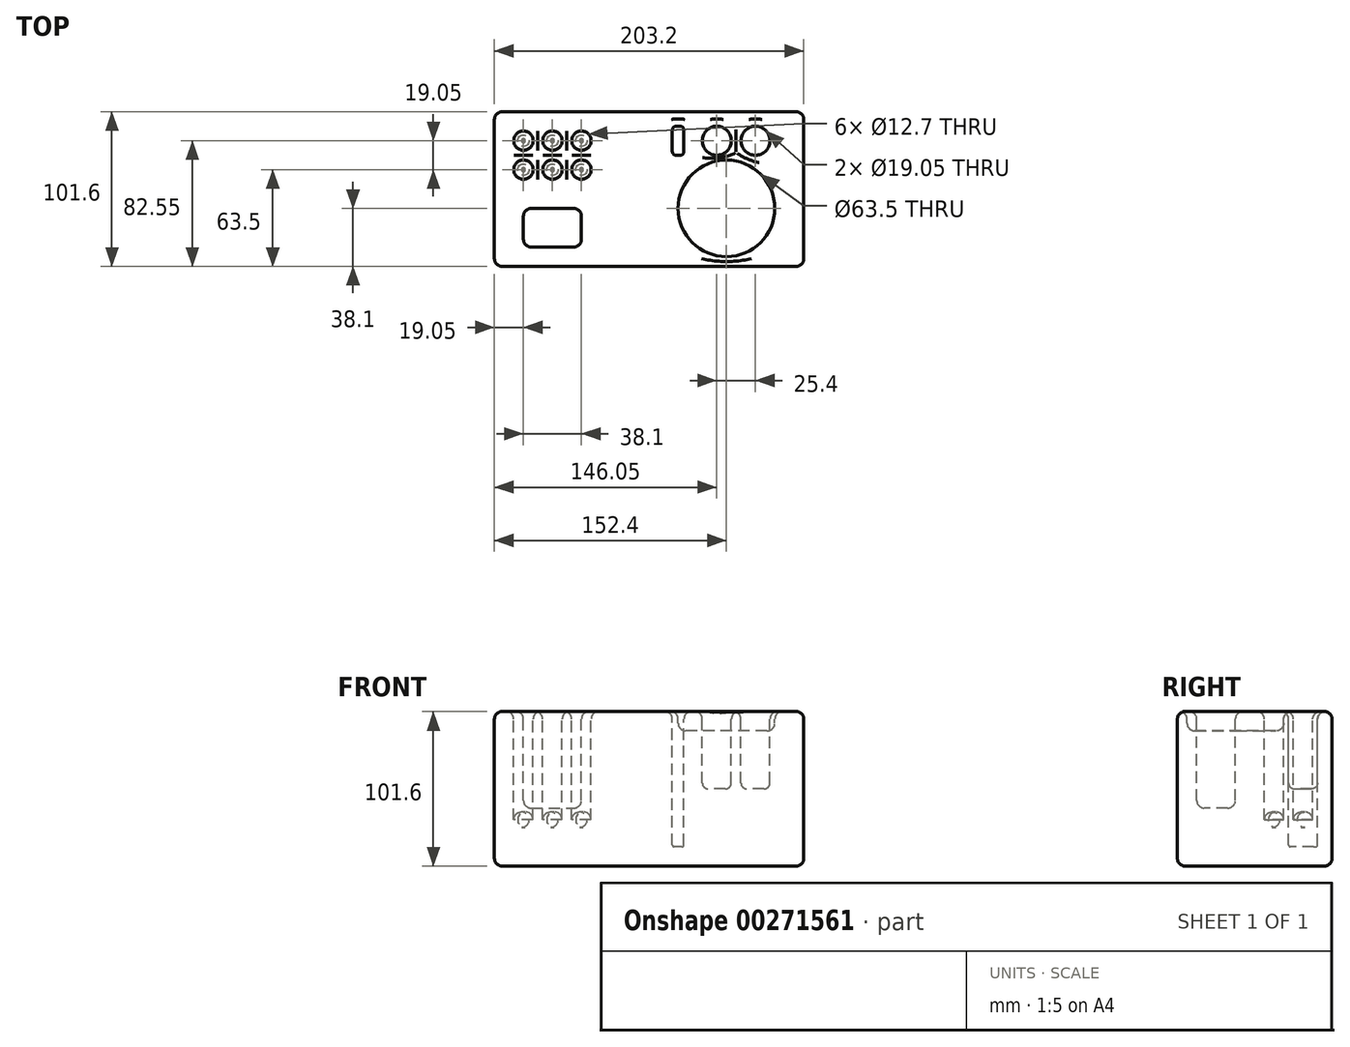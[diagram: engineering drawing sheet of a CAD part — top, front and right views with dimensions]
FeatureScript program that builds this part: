
annotation { "Feature Type Name" : "Feature", "Feature Type Description" : "" }
export const myFeature = defineFeature(function(context is Context, id is Id, definition is map)
    precondition{}
    {
        {
            var Q0;
            Q0=qCreatedBy(makeId("Top.planeOp"),FACE);
            var sketch = newSketch(context, id + "F0", { "sketchPlane" : qUnion([Q0])});
            skLineSegment(sketch, "E0.bottom", {"start": v(0, 0) * mm, "end": v(-203.2, 0) * mm});
            skLineSegment(sketch, "E0.top", {"start": v(0, 101.6) * mm, "end": v(-203.2, 101.6) * mm});
            skLineSegment(sketch, "E0.left", {"start": v(0, 0) * mm, "end": v(0, 101.6) * mm});
            skLineSegment(sketch, "E0.right", {"start": v(-203.2, 0) * mm, "end": v(-203.2, 101.6) * mm});
            skPoint(sketch, "E1", {"position": v(-165.1, 101.6) * mm});
            skPoint(sketch, "E2", {"position": v(-146.05, 101.6) * mm});
            skPoint(sketch, "E3", {"position": v(-184.15, 101.6) * mm});
            skPoint(sketch, "E4", {"position": v(-101.6, 101.6) * mm});
            skPoint(sketch, "E5", {"position": v(-203.2, 82.55) * mm});
            skPoint(sketch, "E6", {"position": v(-203.2, 63.5) * mm});
            skCircle(sketch, "E7", {"center": v(-184.15, 82.55) * mm, "radius": 6.35 * mm});
            skCircle(sketch, "E8", {"center": v(-165.1, 63.5) * mm, "radius": 6.35 * mm});
            skCircle(sketch, "E9", {"center": v(-165.1, 82.55) * mm, "radius": 6.35 * mm});
            skCircle(sketch, "E10", {"center": v(-146.05, 82.55) * mm, "radius": 6.35 * mm});
            skCircle(sketch, "E11", {"center": v(-146.05, 63.5) * mm, "radius": 6.35 * mm});
            skCircle(sketch, "E12", {"center": v(-184.15, 63.5) * mm, "radius": 6.35 * mm});
            skPoint(sketch, "E13", {"position": v(-203.2, 12.7) * mm});
            skPoint(sketch, "E14", {"position": v(-203.2, 38.1) * mm});
            skPoint(sketch, "E15", {"position": v(-184.15, 38.1) * mm});
            skPoint(sketch, "E16", {"position": v(-146.05, 12.7) * mm});
            skLineSegment(sketch, "E17.bottom", {"start": v(-184.15, 38.1) * mm, "end": v(-146.05, 38.1) * mm});
            skLineSegment(sketch, "E17.top", {"start": v(-184.15, 12.7) * mm, "end": v(-146.05, 12.7) * mm});
            skLineSegment(sketch, "E17.left", {"start": v(-184.15, 38.1) * mm, "end": v(-184.15, 12.7) * mm});
            skLineSegment(sketch, "E17.right", {"start": v(-146.05, 38.1) * mm, "end": v(-146.05, 12.7) * mm});
            skPoint(sketch, "E18", {"position": v(-82.55, 101.6) * mm});
            skPoint(sketch, "E19", {"position": v(-82.55, 82.55) * mm});
            skLineSegment(sketch, "E20.bottom", {"start": v(-78.74, 92.07) * mm, "end": v(-86.36, 92.07) * mm});
            skLineSegment(sketch, "E20.top", {"start": v(-78.74, 73.02) * mm, "end": v(-86.36, 73.02) * mm});
            skLineSegment(sketch, "E20.left", {"start": v(-78.74, 92.07) * mm, "end": v(-78.74, 73.02) * mm});
            skLineSegment(sketch, "E20.right", {"start": v(-86.36, 92.07) * mm, "end": v(-86.36, 73.02) * mm});
            skPoint(sketch, "E21", {"position": v(-57.15, 101.6) * mm});
            skPoint(sketch, "E22", {"position": v(-31.75, 101.6) * mm});
            skCircle(sketch, "E23", {"center": v(-57.15, 82.55) * mm, "radius": 9.53 * mm});
            skPoint(sketch, "E23.centerSnap0", {"position": v(-78.74, 82.55) * mm});
            skCircle(sketch, "E24", {"center": v(-31.75, 82.55) * mm, "radius": 9.53 * mm});
            skPoint(sketch, "E25", {"position": v(-50.8, 101.6) * mm});
            skPoint(sketch, "E26", {"position": v(0, 38.1) * mm});
            skCircle(sketch, "E27", {"center": v(-50.8, 38.1) * mm, "radius": 31.75 * mm});
            skSolve(sketch);
        }
        {
            var Q0;
            Q0=makeQuery(id+"F0.imprint","IMPRINT",FACE,{"disambiguationData":[TD([[makeQuery(id+"F0.imprint","IMPRINT",EDGE,{"derivedFrom":sQuery(id+"F0.wireOp",EDGE,"E0.bottom")}),-1.0]])]});
            var Q1;
            Q1=makeQuery(id+"F0.imprint","IMPRINT",FACE,{"disambiguationData":[TD([[makeQuery(id+"F0.imprint","IMPRINT",EDGE,{"derivedFrom":sQuery(id+"F0.wireOp",EDGE,"E9")}),1.0]])]});
            var Q2;
            Q2=makeQuery(id+"F0.imprint","IMPRINT",FACE,{"disambiguationData":[TD([[makeQuery(id+"F0.imprint","IMPRINT",EDGE,{"derivedFrom":sQuery(id+"F0.wireOp",EDGE,"E7")}),1.0]])]});
            var Q3;
            Q3=makeQuery(id+"F0.imprint","IMPRINT",FACE,{"disambiguationData":[TD([[makeQuery(id+"F0.imprint","IMPRINT",EDGE,{"derivedFrom":sQuery(id+"F0.wireOp",EDGE,"E8")}),1.0]])]});
            var Q4;
            Q4=makeQuery(id+"F0.imprint","IMPRINT",FACE,{"disambiguationData":[TD([[makeQuery(id+"F0.imprint","IMPRINT",EDGE,{"derivedFrom":sQuery(id+"F0.wireOp",EDGE,"E12")}),1.0]])]});
            var Q5;
            Q5=makeQuery(id+"F0.imprint","IMPRINT",FACE,{"disambiguationData":[TD([[makeQuery(id+"F0.imprint","IMPRINT",EDGE,{"derivedFrom":sQuery(id+"F0.wireOp",EDGE,"E11")}),1.0]])]});
            var Q6;
            Q6=makeQuery(id+"F0.imprint","IMPRINT",FACE,{"disambiguationData":[TD([[makeQuery(id+"F0.imprint","IMPRINT",EDGE,{"derivedFrom":sQuery(id+"F0.wireOp",EDGE,"E10")}),1.0]])]});
            var Q7;
            Q7=makeQuery(id+"F0.imprint","IMPRINT",FACE,{"disambiguationData":[TD([[makeQuery(id+"F0.imprint","IMPRINT",EDGE,{"derivedFrom":sQuery(id+"F0.wireOp",EDGE,"E17.bottom")}),-1.0]])]});
            var Q8;
            Q8=makeQuery(id+"F0.imprint","IMPRINT",FACE,{"disambiguationData":[TD([[makeQuery(id+"F0.imprint","IMPRINT",EDGE,{"derivedFrom":sQuery(id+"F0.wireOp",EDGE,"E27")}),1.0]])]});
            var Q9;
            Q9=makeQuery(id+"F0.imprint","IMPRINT",FACE,{"disambiguationData":[TD([[makeQuery(id+"F0.imprint","IMPRINT",EDGE,{"derivedFrom":sQuery(id+"F0.wireOp",EDGE,"E23")}),1.0]])]});
            var Q10;
            Q10=makeQuery(id+"F0.imprint","IMPRINT",FACE,{"disambiguationData":[TD([[makeQuery(id+"F0.imprint","IMPRINT",EDGE,{"derivedFrom":sQuery(id+"F0.wireOp",EDGE,"E24")}),1.0]])]});
            var Q11;
            Q11=makeQuery(id+"F0.imprint","IMPRINT",FACE,{"disambiguationData":[TD([[makeQuery(id+"F0.imprint","IMPRINT",EDGE,{"derivedFrom":sQuery(id+"F0.wireOp",EDGE,"E20.bottom")}),1.0]])]});
            extrude(context, id + "F1", {"entities" : qUnion([Q0, Q1, Q2, Q3, Q4, Q5, Q6, Q7, Q8, Q9, Q10, Q11]), "oppositeDirection" : true, "depth" : 101.6 * mm});
        }
        {
            var Q0;
            Q0=makeQuery(id+"F0.imprint","IMPRINT",FACE,{"disambiguationData":[TD([[makeQuery(id+"F0.imprint","IMPRINT",EDGE,{"derivedFrom":sQuery(id+"F0.wireOp",EDGE,"E27")}),1.0]])]});
            extrude(context, id + "F2", {"entities" : qUnion([Q0]), "operationType" : NewBodyOperationType.REMOVE, "oppositeDirection" : true, "depth" : 12.7 * mm});
        }
        {
            var Q0;
            Q0=makeQuery(id+"F0.imprint","IMPRINT",FACE,{"disambiguationData":[TD([[makeQuery(id+"F0.imprint","IMPRINT",EDGE,{"derivedFrom":sQuery(id+"F0.wireOp",EDGE,"E23")}),1.0]])]});
            var Q1;
            Q1=makeQuery(id+"F0.imprint","IMPRINT",FACE,{"disambiguationData":[TD([[makeQuery(id+"F0.imprint","IMPRINT",EDGE,{"derivedFrom":sQuery(id+"F0.wireOp",EDGE,"E24")}),1.0]])]});
            extrude(context, id + "F3", {"entities" : qUnion([Q0, Q1]), "operationType" : NewBodyOperationType.REMOVE, "oppositeDirection" : true, "depth" : 50.8 * mm});
        }
        {
            var Q0;
            Q0=makeQuery(id+"F0.imprint","IMPRINT",FACE,{"disambiguationData":[TD([[makeQuery(id+"F0.imprint","IMPRINT",EDGE,{"derivedFrom":sQuery(id+"F0.wireOp",EDGE,"E20.bottom")}),1.0]])]});
            extrude(context, id + "F4", {"entities" : qUnion([Q0]), "operationType" : NewBodyOperationType.REMOVE, "oppositeDirection" : true, "depth" : 88.9 * mm});
        }
        {
            var Q0;
            Q0=makeQuery(id+"F0.imprint","IMPRINT",FACE,{"disambiguationData":[TD([[makeQuery(id+"F0.imprint","IMPRINT",EDGE,{"derivedFrom":sQuery(id+"F0.wireOp",EDGE,"E12")}),1.0]])]});
            var Q1;
            Q1=makeQuery(id+"F0.imprint","IMPRINT",FACE,{"disambiguationData":[TD([[makeQuery(id+"F0.imprint","IMPRINT",EDGE,{"derivedFrom":sQuery(id+"F0.wireOp",EDGE,"E7")}),1.0]])]});
            var Q2;
            Q2=makeQuery(id+"F0.imprint","IMPRINT",FACE,{"disambiguationData":[TD([[makeQuery(id+"F0.imprint","IMPRINT",EDGE,{"derivedFrom":sQuery(id+"F0.wireOp",EDGE,"E8")}),1.0]])]});
            var Q3;
            Q3=makeQuery(id+"F0.imprint","IMPRINT",FACE,{"disambiguationData":[TD([[makeQuery(id+"F0.imprint","IMPRINT",EDGE,{"derivedFrom":sQuery(id+"F0.wireOp",EDGE,"E10")}),1.0]])]});
            var Q4;
            Q4=makeQuery(id+"F0.imprint","IMPRINT",FACE,{"disambiguationData":[TD([[makeQuery(id+"F0.imprint","IMPRINT",EDGE,{"derivedFrom":sQuery(id+"F0.wireOp",EDGE,"E11")}),1.0]])]});
            var Q5;
            Q5=makeQuery(id+"F0.imprint","IMPRINT",FACE,{"disambiguationData":[TD([[makeQuery(id+"F0.imprint","IMPRINT",EDGE,{"derivedFrom":sQuery(id+"F0.wireOp",EDGE,"E9")}),1.0]])]});
            extrude(context, id + "F5", {"entities" : qUnion([Q0, Q1, Q2, Q3, Q4, Q5]), "operationType" : NewBodyOperationType.REMOVE, "oppositeDirection" : true, "depth" : 76.2 * mm});
        }
        {
            var Q0;
            Q0=makeQuery(id+"F0.imprint","IMPRINT",FACE,{"disambiguationData":[TD([[makeQuery(id+"F0.imprint","IMPRINT",EDGE,{"derivedFrom":sQuery(id+"F0.wireOp",EDGE,"E17.bottom")}),-1.0]])]});
            extrude(context, id + "F6", {"entities" : qUnion([Q0]), "operationType" : NewBodyOperationType.REMOVE, "oppositeDirection" : true, "depth" : 63.5 * mm});
        }
        {
            var Q0;
            Q0=makeQuery(id+"F2.boolean.opBoolean","COPY",EDGE,{"derivedFrom":makeQuery(id+"F2.opExtrude","CAP_EDGE",EDGE,{"disambiguationData":[OSD([sQuery(id+"F0.wireOp",EDGE,"E27")])],"isStart":false})});
            fillet(context, id + "F7", {"entities" : qUnion([Q0]), "radius" : 5.08 * mm, "tangentPropagation" : true, "allowEdgeOverflow" : false});
        }
        {
            var Q0;
            Q0=makeQuery(id+"F5.boolean.opBoolean","COPY",EDGE,{"derivedFrom":makeQuery(id+"F5.opExtrude","CAP_EDGE",EDGE,{"disambiguationData":[OSD([sQuery(id+"F0.wireOp",EDGE,"E7")])],"isStart":false})});
            var Q1;
            Q1=makeQuery(id+"F5.boolean.opBoolean","COPY",EDGE,{"derivedFrom":makeQuery(id+"F5.opExtrude","CAP_EDGE",EDGE,{"disambiguationData":[OSD([sQuery(id+"F0.wireOp",EDGE,"E9")])],"isStart":false})});
            var Q2;
            Q2=makeQuery(id+"F5.boolean.opBoolean","COPY",EDGE,{"derivedFrom":makeQuery(id+"F5.opExtrude","CAP_EDGE",EDGE,{"disambiguationData":[OSD([sQuery(id+"F0.wireOp",EDGE,"E10")])],"isStart":false})});
            var Q3;
            Q3=makeQuery(id+"F5.boolean.opBoolean","COPY",EDGE,{"derivedFrom":makeQuery(id+"F5.opExtrude","CAP_EDGE",EDGE,{"disambiguationData":[OSD([sQuery(id+"F0.wireOp",EDGE,"E11")])],"isStart":false})});
            var Q4;
            Q4=makeQuery(id+"F5.boolean.opBoolean","COPY",EDGE,{"derivedFrom":makeQuery(id+"F5.opExtrude","CAP_EDGE",EDGE,{"disambiguationData":[OSD([sQuery(id+"F0.wireOp",EDGE,"E8")])],"isStart":false})});
            var Q5;
            Q5=makeQuery(id+"F5.boolean.opBoolean","COPY",EDGE,{"derivedFrom":makeQuery(id+"F5.opExtrude","CAP_EDGE",EDGE,{"disambiguationData":[OSD([sQuery(id+"F0.wireOp",EDGE,"E12")])],"isStart":false})});
            fillet(context, id + "F8", {"entities" : qUnion([Q0, Q1, Q2, Q3, Q4, Q5]), "radius" : 5.08 * mm, "tangentPropagation" : true, "allowEdgeOverflow" : false});
        }
        {
            var Q0;
            Q0=makeQuery(id+"F6.boolean.opBoolean","COPY",EDGE,{"derivedFrom":makeQuery(id+"F6.opExtrude","CAP_EDGE",EDGE,{"disambiguationData":[OSD([sQuery(id+"F0.wireOp",EDGE,"E17.right")])],"isStart":false})});
            var Q1;
            Q1=makeQuery(id+"F6.boolean.opBoolean","COPY",EDGE,{"derivedFrom":makeQuery(id+"F6.opExtrude","CAP_EDGE",EDGE,{"disambiguationData":[OSD([sQuery(id+"F0.wireOp",EDGE,"E17.bottom")])],"isStart":false})});
            var Q2;
            Q2=makeQuery(id+"F6.boolean.opBoolean","COPY",EDGE,{"derivedFrom":makeQuery(id+"F6.opExtrude","CAP_EDGE",EDGE,{"disambiguationData":[OSD([sQuery(id+"F0.wireOp",EDGE,"E17.left")])],"isStart":false})});
            var Q3;
            Q3=makeQuery(id+"F6.boolean.opBoolean","COPY",EDGE,{"derivedFrom":makeQuery(id+"F6.opExtrude","CAP_EDGE",EDGE,{"disambiguationData":[OSD([sQuery(id+"F0.wireOp",EDGE,"E17.top")])],"isStart":false})});
            var Q4;
            Q4=makeQuery(id+"F6.boolean.opBoolean","COPY",EDGE,{"derivedFrom":makeQuery(id+"F6.opExtrude","SWEPT_EDGE",EDGE,{"disambiguationData":[OSD([sQuery(id+"F0.wireOp",EDGE,"E17.bottom"),sQuery(id+"F0.wireOp",EDGE,"E17.right")])]})});
            var Q5;
            Q5=makeQuery(id+"F6.boolean.opBoolean","COPY",EDGE,{"derivedFrom":makeQuery(id+"F6.opExtrude","SWEPT_EDGE",EDGE,{"disambiguationData":[OSD([sQuery(id+"F0.wireOp",EDGE,"E17.top"),sQuery(id+"F0.wireOp",EDGE,"E17.right")])]})});
            var Q6;
            Q6=makeQuery(id+"F6.boolean.opBoolean","COPY",EDGE,{"derivedFrom":makeQuery(id+"F6.opExtrude","SWEPT_EDGE",EDGE,{"disambiguationData":[OSD([sQuery(id+"F0.wireOp",EDGE,"E17.top"),sQuery(id+"F0.wireOp",EDGE,"E17.left")])]})});
            var Q7;
            Q7=makeQuery(id+"F6.boolean.opBoolean","COPY",EDGE,{"derivedFrom":makeQuery(id+"F6.opExtrude","SWEPT_EDGE",EDGE,{"disambiguationData":[OSD([sQuery(id+"F0.wireOp",EDGE,"E17.bottom"),sQuery(id+"F0.wireOp",EDGE,"E17.left")])]})});
            fillet(context, id + "F9", {"entities" : qUnion([Q0, Q1, Q2, Q3, Q4, Q5, Q6, Q7]), "radius" : 5.08 * mm, "tangentPropagation" : true, "allowEdgeOverflow" : false});
        }
        {
            var Q0;
            Q0=makeQuery(id+"F3.boolean.opBoolean","COPY",EDGE,{"derivedFrom":makeQuery(id+"F3.opExtrude","CAP_EDGE",EDGE,{"disambiguationData":[OSD([sQuery(id+"F0.wireOp",EDGE,"E23")])],"isStart":false})});
            var Q1;
            Q1=makeQuery(id+"F3.boolean.opBoolean","COPY",EDGE,{"derivedFrom":makeQuery(id+"F3.opExtrude","CAP_EDGE",EDGE,{"disambiguationData":[OSD([sQuery(id+"F0.wireOp",EDGE,"E24")])],"isStart":false})});
            fillet(context, id + "F10", {"entities" : qUnion([Q0, Q1]), "radius" : 3.8 * mm, "tangentPropagation" : true, "allowEdgeOverflow" : false});
        }
        {
            var Q0;
            Q0=makeQuery(id+"F4.boolean.opBoolean","COPY",EDGE,{"derivedFrom":makeQuery(id+"F4.opExtrude","CAP_EDGE",EDGE,{"disambiguationData":[OSD([sQuery(id+"F0.wireOp",EDGE,"E20.right")])],"isStart":false})});
            var Q1;
            Q1=makeQuery(id+"F4.boolean.opBoolean","COPY",EDGE,{"derivedFrom":makeQuery(id+"F4.opExtrude","CAP_EDGE",EDGE,{"disambiguationData":[OSD([sQuery(id+"F0.wireOp",EDGE,"E20.top")])],"isStart":false})});
            var Q2;
            Q2=makeQuery(id+"F4.boolean.opBoolean","COPY",EDGE,{"derivedFrom":makeQuery(id+"F4.opExtrude","CAP_EDGE",EDGE,{"disambiguationData":[OSD([sQuery(id+"F0.wireOp",EDGE,"E20.left")])],"isStart":false})});
            var Q3;
            Q3=makeQuery(id+"F4.boolean.opBoolean","COPY",EDGE,{"derivedFrom":makeQuery(id+"F4.opExtrude","CAP_EDGE",EDGE,{"disambiguationData":[OSD([sQuery(id+"F0.wireOp",EDGE,"E20.bottom")])],"isStart":false})});
            fillet(context, id + "F11", {"entities" : qUnion([Q0, Q1, Q2, Q3]), "radius" : 1.27 * mm, "tangentPropagation" : true, "allowEdgeOverflow" : false});
        }
        {
            var Q0;
            Q0=makeQuery(id+"F5.boolean.opBoolean","COPY",EDGE,{"derivedFrom":makeQuery(id+"F5.opExtrude","CAP_EDGE",EDGE,{"disambiguationData":[OSD([sQuery(id+"F0.wireOp",EDGE,"E7")])],"isStart":true})});
            var Q1;
            Q1=makeQuery(id+"F5.boolean.opBoolean","COPY",EDGE,{"derivedFrom":makeQuery(id+"F5.opExtrude","CAP_EDGE",EDGE,{"disambiguationData":[OSD([sQuery(id+"F0.wireOp",EDGE,"E12")])],"isStart":true})});
            var Q2;
            Q2=makeQuery(id+"F5.boolean.opBoolean","COPY",EDGE,{"derivedFrom":makeQuery(id+"F5.opExtrude","CAP_EDGE",EDGE,{"disambiguationData":[OSD([sQuery(id+"F0.wireOp",EDGE,"E9")])],"isStart":true})});
            var Q3;
            Q3=makeQuery(id+"F5.boolean.opBoolean","COPY",EDGE,{"derivedFrom":makeQuery(id+"F5.opExtrude","CAP_EDGE",EDGE,{"disambiguationData":[OSD([sQuery(id+"F0.wireOp",EDGE,"E8")])],"isStart":true})});
            var Q4;
            Q4=makeQuery(id+"F5.boolean.opBoolean","COPY",EDGE,{"derivedFrom":makeQuery(id+"F5.opExtrude","CAP_EDGE",EDGE,{"disambiguationData":[OSD([sQuery(id+"F0.wireOp",EDGE,"E10")])],"isStart":true})});
            var Q5;
            Q5=makeQuery(id+"F5.boolean.opBoolean","COPY",EDGE,{"derivedFrom":makeQuery(id+"F5.opExtrude","CAP_EDGE",EDGE,{"disambiguationData":[OSD([sQuery(id+"F0.wireOp",EDGE,"E11")])],"isStart":true})});
            var Q6;
            Q6=makeQuery(id+"F6.boolean.opBoolean","COPY",EDGE,{"derivedFrom":makeQuery(id+"F6.opExtrude","CAP_EDGE",EDGE,{"disambiguationData":[OSD([sQuery(id+"F0.wireOp",EDGE,"E17.bottom")])],"isStart":true})});
            var Q7;
            Q7=makeQuery(id+"F9.opFillet","BLEND_EDGE",EDGE,{"blendedFrom":[makeQuery(id+"F6.boolean.opBoolean","COPY",EDGE,{"derivedFrom":makeQuery(id+"F6.opExtrude","SWEPT_EDGE",EDGE,{"disambiguationData":[OSD([sQuery(id+"F0.wireOp",EDGE,"E17.bottom"),sQuery(id+"F0.wireOp",EDGE,"E17.right")])]})}),makeQuery(id+"F1.opExtrude","CAP_FACE",FACE,{"disambiguationData":[OSD([sQuery(id+"F0.wireOp",EDGE,"E0.bottom"),sQuery(id+"F0.wireOp",EDGE,"E0.top"),sQuery(id+"F0.wireOp",EDGE,"E0.left"),sQuery(id+"F0.wireOp",EDGE,"E0.right")])],"isStart":true})],"blendedInto":[makeQuery(id+"F1.opExtrude","CAP_FACE",FACE,{"disambiguationData":[OSD([sQuery(id+"F0.wireOp",EDGE,"E0.bottom"),sQuery(id+"F0.wireOp",EDGE,"E0.top"),sQuery(id+"F0.wireOp",EDGE,"E0.left"),sQuery(id+"F0.wireOp",EDGE,"E0.right")])],"isStart":true})]});
            var Q8;
            Q8=makeQuery(id+"F4.boolean.opBoolean","COPY",EDGE,{"derivedFrom":makeQuery(id+"F4.opExtrude","CAP_EDGE",EDGE,{"disambiguationData":[OSD([sQuery(id+"F0.wireOp",EDGE,"E20.left")])],"isStart":true})});
            var Q9;
            Q9=makeQuery(id+"F4.boolean.opBoolean","COPY",EDGE,{"derivedFrom":makeQuery(id+"F4.opExtrude","CAP_EDGE",EDGE,{"disambiguationData":[OSD([sQuery(id+"F0.wireOp",EDGE,"E20.bottom")])],"isStart":true})});
            var Q10;
            Q10=makeQuery(id+"F4.boolean.opBoolean","COPY",EDGE,{"derivedFrom":makeQuery(id+"F4.opExtrude","CAP_EDGE",EDGE,{"disambiguationData":[OSD([sQuery(id+"F0.wireOp",EDGE,"E20.right")])],"isStart":true})});
            var Q11;
            Q11=makeQuery(id+"F4.boolean.opBoolean","COPY",EDGE,{"derivedFrom":makeQuery(id+"F4.opExtrude","CAP_EDGE",EDGE,{"disambiguationData":[OSD([sQuery(id+"F0.wireOp",EDGE,"E20.top")])],"isStart":true})});
            var Q12;
            Q12=makeQuery(id+"F3.boolean.opBoolean","COPY",EDGE,{"derivedFrom":makeQuery(id+"F3.opExtrude","CAP_EDGE",EDGE,{"disambiguationData":[OSD([sQuery(id+"F0.wireOp",EDGE,"E23")])],"isStart":true})});
            var Q13;
            Q13=makeQuery(id+"F3.boolean.opBoolean","COPY",EDGE,{"derivedFrom":makeQuery(id+"F3.opExtrude","CAP_EDGE",EDGE,{"disambiguationData":[OSD([sQuery(id+"F0.wireOp",EDGE,"E24")])],"isStart":true})});
            var Q14;
            Q14=makeQuery(id+"F2.boolean.opBoolean","COPY",EDGE,{"derivedFrom":makeQuery(id+"F2.opExtrude","CAP_EDGE",EDGE,{"disambiguationData":[OSD([sQuery(id+"F0.wireOp",EDGE,"E27")])],"isStart":true})});
            fillet(context, id + "F12", {"entities" : qUnion([Q0, Q1, Q2, Q3, Q4, Q5, Q6, Q7, Q8, Q9, Q10, Q11, Q12, Q13, Q14]), "radius" : 5.08 * mm, "tangentPropagation" : true, "allowEdgeOverflow" : false});
        }
        {
            var Q0;
            Q0=makeQuery(id+"F4.boolean.opBoolean","COPY",EDGE,{"derivedFrom":makeQuery(id+"F4.opExtrude","SWEPT_EDGE",EDGE,{"disambiguationData":[OSD([sQuery(id+"F0.wireOp",EDGE,"E20.bottom"),sQuery(id+"F0.wireOp",EDGE,"E20.left")])]})});
            var Q1;
            Q1=makeQuery(id+"F4.boolean.opBoolean","COPY",EDGE,{"derivedFrom":makeQuery(id+"F4.opExtrude","SWEPT_EDGE",EDGE,{"disambiguationData":[OSD([sQuery(id+"F0.wireOp",EDGE,"E20.bottom"),sQuery(id+"F0.wireOp",EDGE,"E20.right")])]})});
            var Q2;
            Q2=makeQuery(id+"F4.boolean.opBoolean","COPY",EDGE,{"derivedFrom":makeQuery(id+"F4.opExtrude","SWEPT_EDGE",EDGE,{"disambiguationData":[OSD([sQuery(id+"F0.wireOp",EDGE,"E20.top"),sQuery(id+"F0.wireOp",EDGE,"E20.left")])]})});
            var Q3;
            Q3=makeQuery(id+"F4.boolean.opBoolean","COPY",EDGE,{"derivedFrom":makeQuery(id+"F4.opExtrude","SWEPT_EDGE",EDGE,{"disambiguationData":[OSD([sQuery(id+"F0.wireOp",EDGE,"E20.top"),sQuery(id+"F0.wireOp",EDGE,"E20.right")])]})});
            fillet(context, id + "F13", {"entities" : qUnion([Q0, Q1, Q2, Q3]), "radius" : 2.54 * mm, "tangentPropagation" : true, "allowEdgeOverflow" : false});
        }
        {
            var Q0;
            Q0=makeQuery(id+"F1.opExtrude","SWEPT_FACE",FACE,{"disambiguationData":[OSD([sQuery(id+"F0.wireOp",EDGE,"E0.bottom")])]});
            var Q1;
            Q1=makeQuery(id+"F1.opExtrude","SWEPT_FACE",FACE,{"disambiguationData":[OSD([sQuery(id+"F0.wireOp",EDGE,"E0.right")])]});
            var Q2;
            Q2=makeQuery(id+"F12.opFillet","SPLIT",FACE,{"disambiguationData":[OD(3.0)],"derivedFrom":makeQuery(id+"F1.opExtrude","CAP_FACE",FACE,{"disambiguationData":[OSD([sQuery(id+"F0.wireOp",EDGE,"E0.bottom"),sQuery(id+"F0.wireOp",EDGE,"E0.top"),sQuery(id+"F0.wireOp",EDGE,"E0.left"),sQuery(id+"F0.wireOp",EDGE,"E0.right")])],"isStart":true})});
            var Q3;
            Q3=makeQuery(id+"F1.opExtrude","SWEPT_FACE",FACE,{"disambiguationData":[OSD([sQuery(id+"F0.wireOp",EDGE,"E0.top")])]});
            var Q4;
            Q4=makeQuery(id+"F1.opExtrude","CAP_FACE",FACE,{"disambiguationData":[OSD([sQuery(id+"F0.wireOp",EDGE,"E0.bottom"),sQuery(id+"F0.wireOp",EDGE,"E0.top"),sQuery(id+"F0.wireOp",EDGE,"E0.left"),sQuery(id+"F0.wireOp",EDGE,"E0.right")])],"isStart":false});
            fillet(context, id + "F14", {"entities" : qUnion([Q0, Q1, Q2, Q3, Q4]), "radius" : 5.08 * mm, "tangentPropagation" : true, "allowEdgeOverflow" : false});
        }
    });
